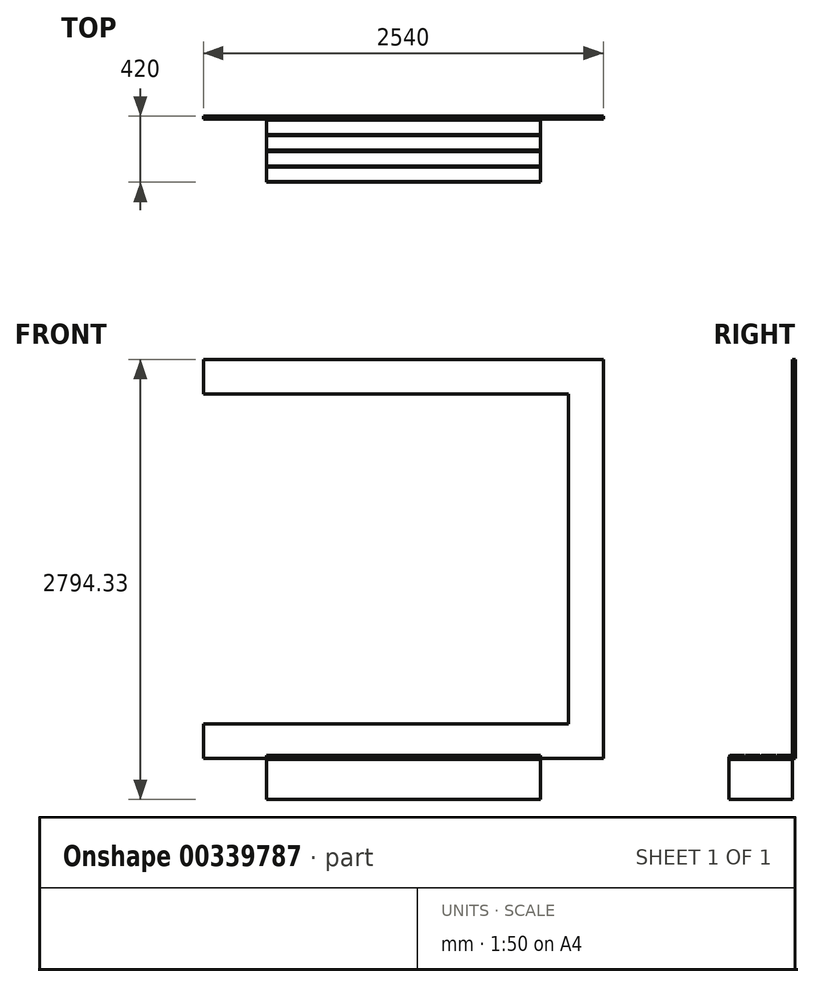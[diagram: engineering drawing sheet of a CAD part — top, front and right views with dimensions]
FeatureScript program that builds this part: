
annotation { "Feature Type Name" : "Feature", "Feature Type Description" : "" }
export const myFeature = defineFeature(function(context is Context, id is Id, definition is map)
    precondition{}
    {
        {
            var Q0;
            Q0=qCreatedBy(makeId("Front.planeOp"),FACE);
            var sketch = newSketch(context, id + "F0", { "sketchPlane" : qUnion([Q0])});
            skLineSegment(sketch, "E0.top", {"start": v(0, 2550) * mm, "end": v(2540, 2550) * mm});
            skLineSegment(sketch, "E0.right", {"start": v(2540, 14.43) * mm, "end": v(2540, 2550) * mm});
            skLineSegment(sketch, "E1.1", {"start": v(2320, 235.67) * mm, "end": v(2320, 2330) * mm});
            skLineSegment(sketch, "E1.2", {"start": v(0, 2330) * mm, "end": v(2320, 2330) * mm});
            skLineSegment(sketch, "E2.trimOffspring", {"start": v(0, 2330) * mm, "end": v(0, 2550) * mm});
            skLineSegment(sketch, "E3.0", {"start": v(0, 14.43) * mm, "end": v(2540, 14.43) * mm});
            skLineSegment(sketch, "E4.0", {"start": v(0, 235.67) * mm, "end": v(2320, 235.67) * mm});
            skLineSegment(sketch, "E5", {"start": v(0, 235.67) * mm, "end": v(0, 14.43) * mm});
            skSolve(sketch);
        }
        {
            var Q0;
            Q0=makeQuery(id+"F0.imprint","IMPRINT",FACE,{"disambiguationData":[TD([[makeQuery(id+"F0.imprint","IMPRINT",EDGE,{"derivedFrom":sQuery(id+"F0.wireOp",EDGE,"E0.top")}),-1.0]])]});
            extrude(context, id + "F1", {"entities" : qUnion([Q0]), "depth" : 20 * mm});
        }
        {
            var Q0;
            Q0=makeQuery(id+"F1.opExtrude","CAP_FACE",FACE,{"disambiguationData":[OSD([sQuery(id+"F0.wireOp",EDGE,"E0.top"),sQuery(id+"F0.wireOp",EDGE,"E0.right"),sQuery(id+"F0.wireOp",EDGE,"E1.1"),sQuery(id+"F0.wireOp",EDGE,"E1.2"),sQuery(id+"F0.wireOp",EDGE,"E2.trimOffspring"),sQuery(id+"F0.wireOp",EDGE,"E3.0"),sQuery(id+"F0.wireOp",EDGE,"E4.0"),sQuery(id+"F0.wireOp",EDGE,"E5")])],"isStart":false});
            var sketch = newSketch(context, id + "F2", { "sketchPlane" : qUnion([Q0])});
            skLineSegment(sketch, "E6.0", {"start": v(400, 35.67) * mm, "end": v(2140, 35.67) * mm});
            skLineSegment(sketch, "E7", {"start": v(400, 35.67) * mm, "end": v(400, -244.33) * mm});
            skLineSegment(sketch, "E8", {"start": v(400, -244.33) * mm, "end": v(2140, -244.33) * mm});
            skLineSegment(sketch, "E9", {"start": v(2140, -244.33) * mm, "end": v(2140, 35.67) * mm});
            skSolve(sketch);
        }
        {
            var Q0;
            {var subQ0=sQuery(id+"F2.wireOp",EDGE,"E6.0");Q0=makeQuery(id+"F2.imprint","IMPRINT",FACE,{"disambiguationData":[TD([[makeQuery(id+"F2.imprint","IMPRINT",EDGE,{"derivedFrom":subQ0}),-1.0]])]});}
            var Q1;
            {var subQ0=sQuery(id+"F2.wireOp",EDGE,"E8");Q1=makeQuery(id+"F2.imprint","IMPRINT",FACE,{"disambiguationData":[TD([[makeQuery(id+"F2.imprint","IMPRINT",EDGE,{"derivedFrom":subQ0}),1.0]])]});}
            extrude(context, id + "F3", {"entities" : qUnion([Q0, Q1]), "depth" : 400 * mm});
        }
        {
            var Q0;
            Q0=makeQuery(id+"F3.opExtrude","SWEPT_FACE",FACE,{"disambiguationData":[OSD([sQuery(id+"F2.wireOp",EDGE,"E7")])]});
            var sketch = newSketch(context, id + "F4", { "sketchPlane" : qUnion([Q0])});
            skLineSegment(sketch, "E10", {"start": v(220, 35.67) * mm, "end": v(420, 35.67) * mm});
            skLineSegment(sketch, "E11", {"start": v(20, 35.67) * mm, "end": v(220, 35.67) * mm});
            skLineSegment(sketch, "E12", {"start": v(120, 25.67) * mm, "end": v(115.6, 35.67) * mm});
            skLineSegment(sketch, "E13", {"start": v(120, 25.67) * mm, "end": v(124.69, 35.67) * mm});
            skLineSegment(sketch, "E14", {"start": v(220, 25.67) * mm, "end": v(215.24, 35.67) * mm});
            skLineSegment(sketch, "E15", {"start": v(220, 25.67) * mm, "end": v(224.71, 35.67) * mm});
            skLineSegment(sketch, "E16", {"start": v(320, 25.67) * mm, "end": v(315.45, 35.67) * mm});
            skLineSegment(sketch, "E17", {"start": v(320, 25.67) * mm, "end": v(324.73, 35.67) * mm});
            skLineSegment(sketch, "E18", {"start": v(324.73, 35.67) * mm, "end": v(315.45, 35.67) * mm});
            skLineSegment(sketch, "E19", {"start": v(224.71, 35.67) * mm, "end": v(215.24, 35.67) * mm});
            skLineSegment(sketch, "E20", {"start": v(124.69, 35.67) * mm, "end": v(115.6, 35.67) * mm});
            skSolve(sketch);
        }
        {
            var Q0;
            Q0=makeQuery(id+"F4.imprint","IMPRINT",FACE,{"disambiguationData":[TD([[makeQuery(id+"F4.imprint","IMPRINT",EDGE,{"derivedFrom":sQuery(id+"F4.wireOp",EDGE,"E16")}),-1.0]])]});
            var Q1;
            Q1=makeQuery(id+"F4.imprint","IMPRINT",FACE,{"disambiguationData":[TD([[makeQuery(id+"F4.imprint","IMPRINT",EDGE,{"derivedFrom":sQuery(id+"F4.wireOp",EDGE,"E14")}),-1.0]])]});
            var Q2;
            Q2=makeQuery(id+"F4.imprint","IMPRINT",FACE,{"disambiguationData":[TD([[makeQuery(id+"F4.imprint","IMPRINT",EDGE,{"derivedFrom":sQuery(id+"F4.wireOp",EDGE,"E12")}),-1.0]])]});
            extrude(context, id + "F5", {"entities" : qUnion([Q0, Q1, Q2]), "operationType" : NewBodyOperationType.REMOVE, "endBound" : BoundingType.UP_TO_NEXT, "oppositeDirection" : true, "depth" : 25 * mm});
        }
        {
            var Q0;
            Q0=makeQuery(id+"F3.opExtrude","CAP_EDGE",EDGE,{"disambiguationData":[OSD([sQuery(id+"F2.wireOp",EDGE,"E6.0")])],"isStart":false});
            chamfer(context, id + "F6", {"entities" : qUnion([Q0]), "chamferType" : ChamferType.TWO_OFFSETS, "width1" : 5 * mm, "oppositeDirection" : false, "width2" : 10 * mm, "tangentPropagation" : true});
        }
        {
            var Q0;
            Q0=makeQuery(id+"F3.opExtrude","CAP_EDGE",EDGE,{"disambiguationData":[OSD([sQuery(id+"F2.wireOp",EDGE,"E6.0")])],"isStart":true});
            chamfer(context, id + "F7", {"entities" : qUnion([Q0]), "chamferType" : ChamferType.TWO_OFFSETS, "width1" : 10 * mm, "oppositeDirection" : false, "width2" : 5 * mm, "tangentPropagation" : true});
        }
        {
            var Q0;
            Q0=makeQuery(id+"F3.opExtrude","CAP_FACE",FACE,{"disambiguationData":[OSD([sQuery(id+"F2.wireOp",EDGE,"E6.0"),sQuery(id+"F2.wireOp",EDGE,"E7"),sQuery(id+"F2.wireOp",EDGE,"E8"),sQuery(id+"F2.wireOp",EDGE,"E9")])],"isStart":false});
            var sketch = newSketch(context, id + "F8", { "sketchPlane" : qUnion([Q0])});
            skLineSegment(sketch, "E21", {"start": v(400, 13.98) * mm, "end": v(410, 13.98) * mm});
            skLineSegment(sketch, "E22", {"start": v(410, 8.98) * mm, "end": v(400, 8.98) * mm});
            skLineSegment(sketch, "E23", {"start": v(400, 8.98) * mm, "end": v(400, 13.98) * mm});
            skLineSegment(sketch, "E24", {"start": v(400, -244.33) * mm, "end": v(2140, -244.33) * mm, "construction": true});
            skLineSegment(sketch, "E25", {"start": v(1270, -244.33) * mm, "end": v(1270, -95.32) * mm, "construction": true});
            skLineSegment(sketch, "E26.MirrorCS", {"start": v(2140, 13.98) * mm, "end": v(2130, 13.98) * mm});
            skLineSegment(sketch, "E27.MirrorCS", {"start": v(2130, 8.98) * mm, "end": v(2140, 8.98) * mm});
            skLineSegment(sketch, "E28.MirrorCS", {"start": v(2140, 8.98) * mm, "end": v(2140, 13.98) * mm});
            skLineSegment(sketch, "E29", {"start": v(410, 13.98) * mm, "end": v(2130, 13.98) * mm});
            skLineSegment(sketch, "E30", {"start": v(2130, 8.98) * mm, "end": v(410, 8.98) * mm});
            skSolve(sketch);
        }
        {
            var Q0;
            Q0 = qSketchRegion(id + "F8", true);
            extrude(context, id + "F9", {"entities" : qUnion([Q0]), "operationType" : NewBodyOperationType.REMOVE, "endBound" : BoundingType.UP_TO_NEXT, "oppositeDirection" : true, "depth" : 25 * mm});
        }
    });
